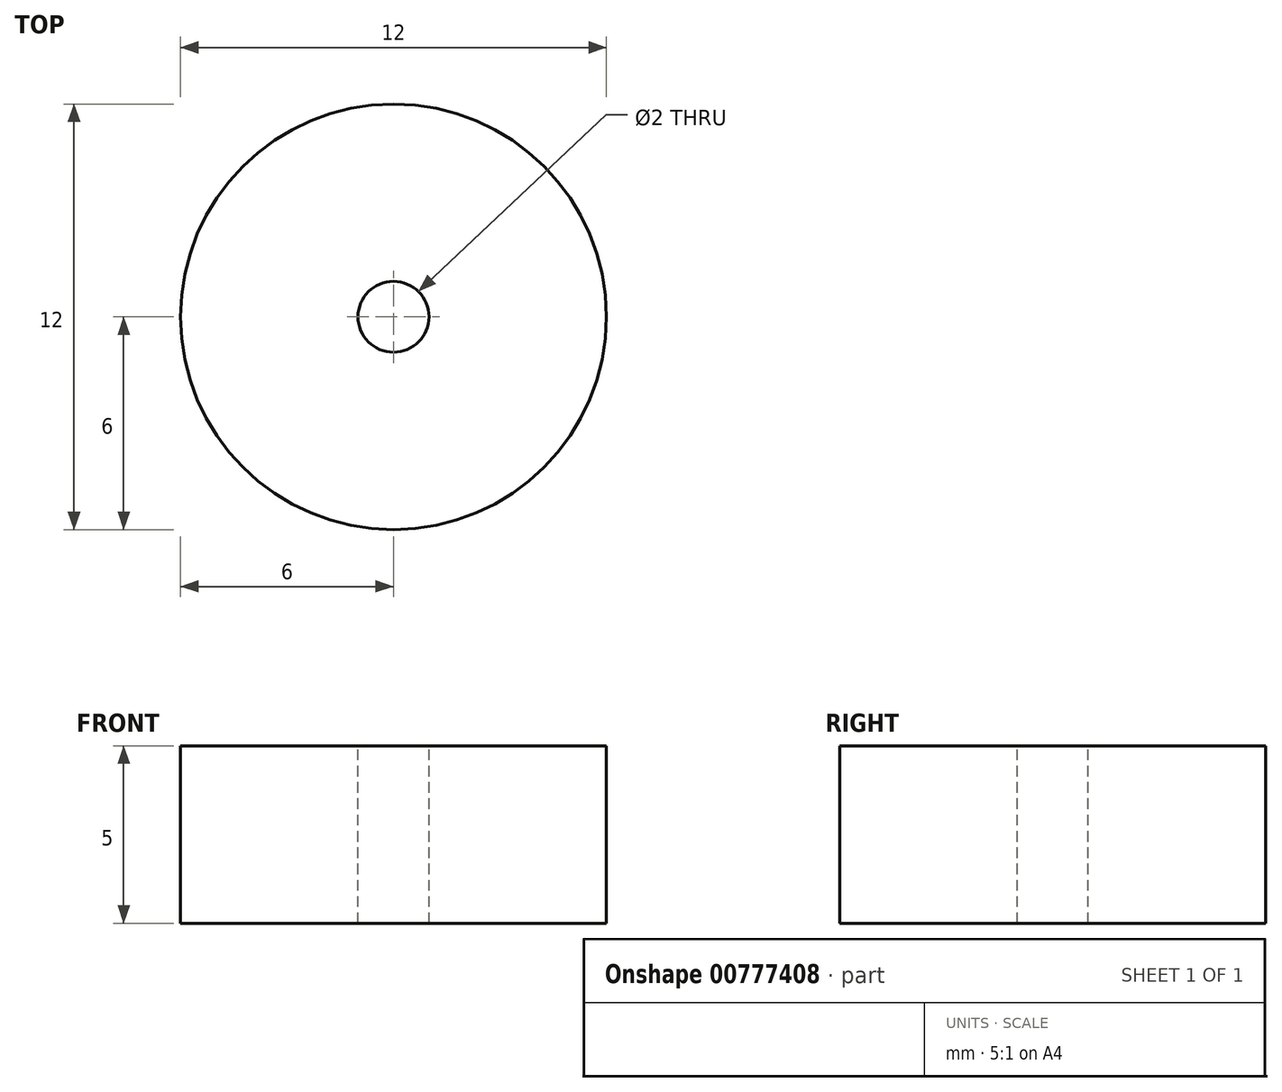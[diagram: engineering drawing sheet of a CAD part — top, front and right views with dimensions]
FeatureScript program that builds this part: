
annotation { "Feature Type Name" : "Feature", "Feature Type Description" : "" }
export const myFeature = defineFeature(function(context is Context, id is Id, definition is map)
    precondition{}
    {
        {
            var Q0;
            Q0=qCreatedBy(makeId("Top.planeOp"),FACE);
            var sketch = newSketch(context, id + "F0", { "sketchPlane" : qUnion([Q0])});
            skCircle(sketch, "E0", {"center": v(0, 0) * mm, "radius": 6 * mm});
            skSolve(sketch);
        }
        {
            var Q0;
            Q0=makeQuery(id+"F0.imprint","IMPRINT",FACE,{"disambiguationData":[TD([[makeQuery(id+"F0.imprint","IMPRINT",EDGE,{"derivedFrom":sQuery(id+"F0.wireOp",EDGE,"E0")}),1.0]])]});
            extrude(context, id + "F1", {"entities" : qUnion([Q0]), "depth" : 5 * mm, "offsetDistance" : 25 * mm});
        }
        {
            var Q0;
            Q0=makeQuery(id+"F1.opExtrude","CAP_FACE",FACE,{"disambiguationData":[OSD([sQuery(id+"F0.wireOp",EDGE,"E0")])],"isStart":false});
            var sketch = newSketch(context, id + "F2", { "sketchPlane" : qUnion([Q0])});
            skCircle(sketch, "E1", {"center": v(0, 0) * mm, "radius": 1 * mm});
            skSolve(sketch);
        }
        {
            var Q0;
            Q0 = qSketchRegion(id + "F2", true);
            extrude(context, id + "F3", {"entities" : qUnion([Q0]), "operationType" : NewBodyOperationType.REMOVE, "endBound" : BoundingType.THROUGH_ALL, "oppositeDirection" : true, "depth" : 25 * mm, "offsetDistance" : 25 * mm});
        }
    });
